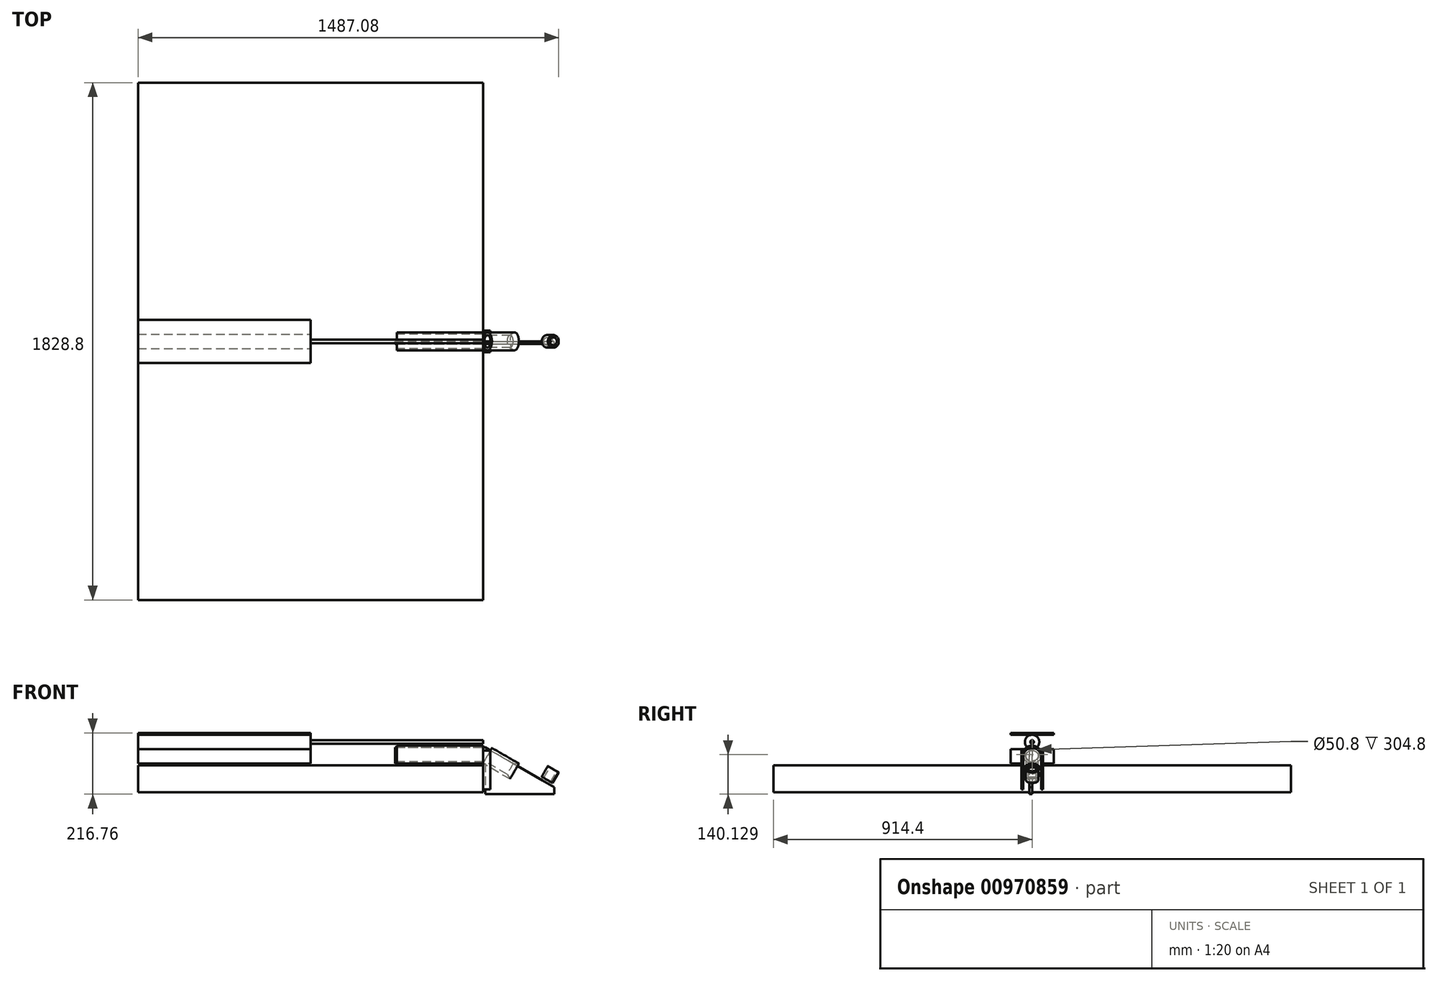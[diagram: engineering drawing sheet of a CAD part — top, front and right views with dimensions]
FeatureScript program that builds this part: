
annotation { "Feature Type Name" : "Feature", "Feature Type Description" : "" }
export const myFeature = defineFeature(function(context is Context, id is Id, definition is map)
    precondition{}
    {
        {
            var Q0;
            Q0=qCreatedBy(makeId("Front.planeOp"),FACE);
            var sketch = newSketch(context, id + "F0", { "sketchPlane" : qUnion([Q0])});
            skLineSegment(sketch, "E0.bottom", {"start": v(-592.75, 52.67) * mm, "end": v(16.85, 52.67) * mm});
            skLineSegment(sketch, "E0.top", {"start": v(-592.75, -48.93) * mm, "end": v(626.45, -48.93) * mm});
            skLineSegment(sketch, "E0.left", {"start": v(-592.75, 52.67) * mm, "end": v(-592.75, -48.93) * mm});
            skLineSegment(sketch, "E0.right", {"start": v(626.45, 52.67) * mm, "end": v(626.45, -48.93) * mm});
            skLineSegment(sketch, "E1.bottom", {"start": v(626.45, 52.67) * mm, "end": v(321.65, 52.67) * mm});
            skLineSegment(sketch, "E1.top", {"start": v(626.45, 116.17) * mm, "end": v(321.65, 116.17) * mm});
            skLineSegment(sketch, "E1.left", {"start": v(626.45, 52.67) * mm, "end": v(626.45, 116.17) * mm});
            skLineSegment(sketch, "E1.right", {"start": v(321.65, 52.67) * mm, "end": v(321.65, 116.17) * mm});
            skLineSegment(sketch, "E2.top", {"start": v(-592.75, 161.05) * mm, "end": v(16.85, 161.05) * mm});
            skLineSegment(sketch, "E2.left", {"start": v(-592.75, 52.67) * mm, "end": v(-592.75, 161.05) * mm});
            skLineSegment(sketch, "E2.right", {"start": v(16.85, 52.67) * mm, "end": v(16.85, 161.05) * mm});
            skLineSegment(sketch, "E3", {"start": v(626.45, 52.67) * mm, "end": v(802.43, -48.93) * mm});
            skLineSegment(sketch, "E4", {"start": v(802.43, -48.93) * mm, "end": v(834.18, 6.06) * mm});
            skLineSegment(sketch, "E5", {"start": v(626.45, 52.67) * mm, "end": v(658.2, 107.66) * mm});
            skLineSegment(sketch, "E6", {"start": v(658.2, 107.66) * mm, "end": v(834.18, 6.06) * mm});
            skLineSegment(sketch, "E7", {"start": v(834.18, 6.06) * mm, "end": v(834.18, 315.51) * mm});
            skLineSegment(sketch, "E8", {"start": v(554.78, 322.17) * mm, "end": v(554.78, 135.22) * mm});
            skLineSegment(sketch, "E9", {"start": v(626.45, 122.52) * mm, "end": v(16.85, 122.52) * mm});
            skLineSegment(sketch, "E10.0", {"start": v(626.45, 135.22) * mm, "end": v(16.85, 135.22) * mm});
            skLineSegment(sketch, "E11.0", {"start": v(665.46, 103.47) * mm, "end": v(655.78, 103.47) * mm});
            skLineSegment(sketch, "E12", {"start": v(16.85, 154.27) * mm, "end": v(16.85, 103.47) * mm});
            skLineSegment(sketch, "E13.trimOffspring", {"start": v(16.85, 154.27) * mm, "end": v(-592.75, 154.27) * mm});
            skLineSegment(sketch, "E14.trimOffspring", {"start": v(16.85, 103.47) * mm, "end": v(-592.75, 103.47) * mm});
            skLineSegment(sketch, "E15", {"start": v(626.45, 116.17) * mm, "end": v(626.45, 116.17) * mm});
            skLineSegment(sketch, "E16", {"start": v(626.45, 122.52) * mm, "end": v(626.45, 135.22) * mm});
            skLineSegment(sketch, "E17", {"start": v(834.18, 6.06) * mm, "end": v(855.85, 43.6) * mm});
            skLineSegment(sketch, "E18", {"start": v(855.85, 43.6) * mm, "end": v(894.18, 21.47) * mm});
            skLineSegment(sketch, "E19", {"start": v(894.18, 21.47) * mm, "end": v(872.45, -16.18) * mm});
            skLineSegment(sketch, "E20", {"start": v(872.45, -16.18) * mm, "end": v(834.18, 6.06) * mm});
            skLineSegment(sketch, "E21", {"start": v(853.31, -5.06) * mm, "end": v(834.18, -38.2) * mm});
            skLineSegment(sketch, "E22.0", {"start": v(-592.75, 46.32) * mm, "end": v(626.45, 46.32) * mm});
            skLineSegment(sketch, "E23.trimOffspring", {"start": v(321.65, 52.67) * mm, "end": v(626.45, 52.67) * mm});
            skLineSegment(sketch, "E24", {"start": v(321.65, 84.42) * mm, "end": v(626.45, 84.42) * mm});
            skLineSegment(sketch, "E25", {"start": v(642.33, 80.17) * mm, "end": v(818.3, -21.43) * mm});
            skLineSegment(sketch, "E26", {"start": v(853.31, -5.06) * mm, "end": v(875.12, 32.47) * mm});
            skLineSegment(sketch, "E27", {"start": v(626.45, 128.87) * mm, "end": v(16.85, 128.87) * mm});
            skLineSegment(sketch, "E28", {"start": v(16.85, 128.87) * mm, "end": v(-592.75, 128.87) * mm});
            skLineSegment(sketch, "E29.0", {"start": v(315.3, 52.67) * mm, "end": v(315.3, 109.82) * mm});
            skLineSegment(sketch, "E30", {"start": v(315.3, 52.67) * mm, "end": v(365.35, 52.67) * mm});
            skLineSegment(sketch, "E31", {"start": v(315.3, 109.82) * mm, "end": v(634.38, 109.82) * mm});
            skLineSegment(sketch, "E32", {"start": v(315.3, 52.67) * mm, "end": v(1006.93, 52.67) * mm});
            skLineSegment(sketch, "E33", {"start": v(634.38, 109.82) * mm, "end": v(634.38, -55.71) * mm});
            skLineSegment(sketch, "E34", {"start": v(880.35, 69.65) * mm, "end": v(877.52, 64.75) * mm});
            skLineSegment(sketch, "E35", {"start": v(877.52, 64.75) * mm, "end": v(779.96, -104.23) * mm});
            skLineSegment(sketch, "E36", {"start": v(634.38, -55.71) * mm, "end": v(824.21, -55.71) * mm});
            skLineSegment(sketch, "E37", {"start": v(634.38, 109.82) * mm, "end": v(836.25, -6.73) * mm});
            skLineSegment(sketch, "E38.0", {"start": v(912.5, 44.56) * mm, "end": v(814.93, -124.42) * mm});
            skLineSegment(sketch, "E39", {"start": v(836.25, -6.73) * mm, "end": v(878.82, -31.47) * mm});
            skLineSegment(sketch, "E40", {"start": v(824.21, -55.71) * mm, "end": v(878.82, -55.71) * mm});
            skLineSegment(sketch, "E41", {"start": v(878.82, -55.71) * mm, "end": v(878.82, -31.47) * mm});
            skSolve(sketch);
        }
        {
            var Q0;
            {var subQ0=sQuery(id+"F0.wireOp",EDGE,"E11.0");Q0=makeQuery(id+"F0.imprint","IMPRINT",FACE,{"disambiguationData":[TD([[makeQuery(id+"F0.imprint","IMPRINT",EDGE,{"derivedFrom":subQ0}),1.0]])]});}
            var Q1;
            {var subQ3=sQuery(id+"F0.wireOp",EDGE,"E11.0");Q1=makeQuery(id+"F0.imprint","IMPRINT",FACE,{"disambiguationData":[TD([[makeQuery(id+"F0.imprint","IMPRINT",EDGE,{"derivedFrom":subQ3}),-1.0]])]});}
            var Q2;
            Q2=sQuery(id+"F0.wireOp",EDGE,"E25");
            revolve(context, id + "F1", {"surfaceOperationType" : NewSurfaceOperationType.NEW, "entities" : qUnion([Q0, Q1]), "axis" : qUnion([Q2]), "revolveType" : RevolveType.FULL});
        }
        {
            var Q0;
            {var subQ0=sQuery(id+"F0.wireOp",EDGE,"E1.top");Q0=makeQuery(id+"F0.imprint","IMPRINT",FACE,{"disambiguationData":[TD([[makeQuery(id+"F0.imprint","IMPRINT",EDGE,{"derivedFrom":subQ0}),1.0]])]});}
            var Q1;
            Q1=sQuery(id+"F0.wireOp",EDGE,"E24");
            revolve(context, id + "F2", {"surfaceOperationType" : NewSurfaceOperationType.NEW, "entities" : qUnion([Q0]), "axis" : qUnion([Q1]), "revolveType" : RevolveType.FULL});
        }
        {
            var Q0;
            {var subQ0=sQuery(id+"F0.wireOp",EDGE,"E17");Q0=makeQuery(id+"F0.imprint","IMPRINT",FACE,{"disambiguationData":[TD([[makeQuery(id+"F0.imprint","IMPRINT",EDGE,{"derivedFrom":subQ0}),-1.0]])]});}
            var Q1;
            Q1=sQuery(id+"F0.wireOp",EDGE,"E26");
            revolve(context, id + "F3", {"surfaceOperationType" : NewSurfaceOperationType.NEW, "entities" : qUnion([Q0]), "axis" : qUnion([Q1]), "revolveType" : RevolveType.FULL});
        }
        {
            var Q0;
            {var subQ3=sQuery(id+"F0.wireOp",EDGE,"E13.trimOffspring");Q0=makeQuery(id+"F0.imprint","IMPRINT",FACE,{"disambiguationData":[TD([[makeQuery(id+"F0.imprint","IMPRINT",EDGE,{"derivedFrom":subQ3}),1.0]])]});}
            var Q1;
            Q1=sQuery(id+"F0.wireOp",EDGE,"E28");
            revolve(context, id + "F4", {"surfaceOperationType" : NewSurfaceOperationType.NEW, "entities" : qUnion([Q0]), "axis" : qUnion([Q1]), "revolveType" : RevolveType.FULL});
        }
        {
            var Q0;
            {var subQ3=sQuery(id+"F0.wireOp",EDGE,"E27");Q0=makeQuery(id+"F0.imprint","IMPRINT",FACE,{"disambiguationData":[TD([[makeQuery(id+"F0.imprint","IMPRINT",EDGE,{"derivedFrom":subQ3}),-1.0]])]});}
            var Q1;
            Q1=sQuery(id+"F0.wireOp",EDGE,"E27");
            revolve(context, id + "F5", {"operationType" : NewBodyOperationType.ADD, "surfaceOperationType" : NewSurfaceOperationType.NEW, "entities" : qUnion([Q0]), "axis" : qUnion([Q1]), "revolveType" : RevolveType.FULL});
        }
        {
            var Q0;
            {var subQ0=sQuery(id+"F0.wireOp",EDGE,"E2.top");Q0=makeQuery(id+"F0.imprint","IMPRINT",FACE,{"disambiguationData":[TD([[makeQuery(id+"F0.imprint","IMPRINT",EDGE,{"derivedFrom":subQ0}),-1.0]])]});}
            var Q1;
            {var subQ0=sQuery(id+"F0.wireOp",EDGE,"E0.bottom");Q1=makeQuery(id+"F0.imprint","IMPRINT",FACE,{"disambiguationData":[TD([[makeQuery(id+"F0.imprint","IMPRINT",EDGE,{"derivedFrom":subQ0}),1.0]])]});}
            extrude(context, id + "F6", {"entities" : qUnion([Q0, Q1]), "operationType" : NewBodyOperationType.ADD, "depth" : 152.4 * mm, "offsetDistance" : 25.4 * mm, "symmetric" : true});
        }
        {
            var Q0;
            {var subQ0=sQuery(id+"F0.wireOp",EDGE,"E0.top");Q0=makeQuery(id+"F0.imprint","IMPRINT",FACE,{"disambiguationData":[TD([[makeQuery(id+"F0.imprint","IMPRINT",EDGE,{"derivedFrom":subQ0}),1.0]])]});}
            extrude(context, id + "F7", {"entities" : qUnion([Q0]), "depth" : 1828.8 * mm, "offsetDistance" : 25.4 * mm, "symmetric" : true});
        }
        {
            var Q0;
            Q0=makeQuery(id+"F2.opRevolve","SWEPT_FACE",FACE,{"disambiguationData":[OSD([sQuery(id+"F0.wireOp",EDGE,"E1.left")])]});
            var sketch = newSketch(context, id + "F8", { "sketchPlane" : qUnion([Q0])});
            skLineSegment(sketch, "E42", {"start": v(31.75, 97.95) * mm, "end": v(31.75, -14.33) * mm});
            skLineSegment(sketch, "E43", {"start": v(-31.75, 97.95) * mm, "end": v(-31.75, -38.39) * mm});
            skLineSegment(sketch, "E44", {"start": v(-31.75, 177.43) * mm, "end": v(-38.1, 177.43) * mm});
            skLineSegment(sketch, "E45", {"start": v(-38.1, 97.95) * mm, "end": v(-38.1, -38.39) * mm});
            skLineSegment(sketch, "E46", {"start": v(31.75, 175.71) * mm, "end": v(38.1, 175.71) * mm});
            skLineSegment(sketch, "E47", {"start": v(38.1, 97.95) * mm, "end": v(38.1, -38.39) * mm});
            skLineSegment(sketch, "E48", {"start": v(31.75, -38.39) * mm, "end": v(31.75, -14.33) * mm});
            skLineSegment(sketch, "E49", {"start": v(38.1, -38.39) * mm, "end": v(31.75, -38.39) * mm});
            skLineSegment(sketch, "E50.trimOffspring", {"start": v(-31.75, -38.39) * mm, "end": v(-38.1, -38.39) * mm});
            skPoint(sketch, "E51.end.orphan", {"position": v(31.75, -54) * mm});
            skLineSegment(sketch, "E52", {"start": v(38.1, 97.95) * mm, "end": v(31.75, 97.95) * mm});
            skLineSegment(sketch, "E53.trimOffspring", {"start": v(-31.75, 97.95) * mm, "end": v(-38.1, 97.95) * mm});
            skSolve(sketch);
        }
        {
            var Q0;
            Q0=makeQuery(id+"F8.imprint","IMPRINT",FACE,{"disambiguationData":[TD([[makeQuery(id+"F8.imprint","IMPRINT",EDGE,{"derivedFrom":sQuery(id+"F8.wireOp",EDGE,"E45")}),1.0]])]});
            var Q1;
            Q1=makeQuery(id+"F8.imprint","IMPRINT",FACE,{"disambiguationData":[TD([[makeQuery(id+"F8.imprint","IMPRINT",EDGE,{"derivedFrom":sQuery(id+"F8.wireOp",EDGE,"E47")}),-1.0]])]});
            extrude(context, id + "F9", {"entities" : qUnion([Q0, Q1]), "depth" : 25.4 * mm, "offsetDistance" : 25.4 * mm});
        }
        {
            var Q0;
            {var subQ0=sQuery(id+"F0.wireOp",EDGE,"E24");Q0=makeQuery(id+"F0.imprint","IMPRINT",FACE,{"disambiguationData":[TD([[makeQuery(id+"F0.imprint","IMPRINT",EDGE,{"derivedFrom":subQ0}),1.0]])]});}
            var Q1;
            {var subQ1=sQuery(id+"F0.wireOp",EDGE,"E29.0");Q1=makeQuery(id+"F0.imprint","IMPRINT",FACE,{"disambiguationData":[TD([[makeQuery(id+"F0.imprint","IMPRINT",EDGE,{"derivedFrom":subQ1}),-1.0]])]});}
            var Q2;
            {var subQ3=sQuery(id+"F0.wireOp",EDGE,"E24");Q2=makeQuery(id+"F0.imprint","IMPRINT",FACE,{"disambiguationData":[TD([[makeQuery(id+"F0.imprint","IMPRINT",EDGE,{"derivedFrom":subQ3}),-1.0]])]});}
            var Q3;
            {var subQ3=sQuery(id+"F0.wireOp",EDGE,"E1.left");var subQ8=makeQuery(id+"F0.imprint","INTERSECT",VERTEX,{"derivedFrom":[subQ3,sQuery(id+"F0.wireOp",EDGE,"E24")]});Q3=makeQuery(id+"F0.imprint","IMPRINT",FACE,{"disambiguationData":[TD([[makeQuery(id+"F0.imprint","IMPRINT",EDGE,{"disambiguationData":[TD([[subQ8,-1.0]])],"derivedFrom":subQ3}),-1.0]])]});}
            var Q4;
            {var subQ0=sQuery(id+"F0.wireOp",EDGE,"E5");var subQ1=makeQuery(id+"F0.imprint","INTERSECT",VERTEX,{"derivedFrom":[subQ0,sQuery(id+"F0.wireOp",EDGE,"E25")]});Q4=makeQuery(id+"F0.imprint","IMPRINT",FACE,{"disambiguationData":[TD([[makeQuery(id+"F0.imprint","IMPRINT",EDGE,{"disambiguationData":[TD([[subQ1,1.0]])],"derivedFrom":subQ0}),1.0]])]});}
            var Q5;
            {var subQ0=sQuery(id+"F0.wireOp",EDGE,"E25");var subQ1=sQuery(id+"F0.wireOp",EDGE,"E5");var subQ2=makeQuery(id+"F0.imprint","INTERSECT",VERTEX,{"derivedFrom":[subQ1,subQ0]});Q5=makeQuery(id+"F0.imprint","IMPRINT",FACE,{"disambiguationData":[TD([[makeQuery(id+"F0.imprint","IMPRINT",EDGE,{"disambiguationData":[TD([[subQ2,-1.0]])],"derivedFrom":subQ1}),-1.0]])]});}
            var Q6;
            {var subQ0=sQuery(id+"F0.wireOp",EDGE,"E25");var subQ1=sQuery(id+"F0.wireOp",EDGE,"E5");var subQ2=makeQuery(id+"F0.imprint","INTERSECT",VERTEX,{"derivedFrom":[subQ1,subQ0]});Q6=makeQuery(id+"F0.imprint","IMPRINT",FACE,{"disambiguationData":[TD([[makeQuery(id+"F0.imprint","IMPRINT",EDGE,{"disambiguationData":[TD([[subQ2,1.0]])],"derivedFrom":subQ1}),-1.0]])]});}
            var Q7;
            {var subQ1=sQuery(id+"F0.wireOp",EDGE,"E5");var subQ3=sQuery(id+"F0.wireOp",EDGE,"E33");var subQ4=makeQuery(id+"F0.imprint","INTERSECT",VERTEX,{"derivedFrom":[subQ1,subQ3]});Q7=makeQuery(id+"F0.imprint","IMPRINT",FACE,{"disambiguationData":[TD([[makeQuery(id+"F0.imprint","IMPRINT",EDGE,{"disambiguationData":[TD([[subQ4,-1.0]])],"derivedFrom":subQ3}),-1.0]])]});}
            var Q8;
            {var subQ0=sQuery(id+"F0.wireOp",EDGE,"E4");var subQ7=sQuery(id+"F0.wireOp",EDGE,"E3");var subQ9=makeQuery(id+"F0.imprint","INTERSECT",VERTEX,{"derivedFrom":[subQ7,subQ0]});Q8=makeQuery(id+"F0.imprint","IMPRINT",FACE,{"disambiguationData":[TD([[makeQuery(id+"F0.imprint","IMPRINT",EDGE,{"disambiguationData":[TD([[subQ9,1.0]])],"derivedFrom":subQ7}),-1.0]])]});}
            var Q9;
            {var subQ5=sQuery(id+"F0.wireOp",EDGE,"E4");var subQ7=sQuery(id+"F0.wireOp",EDGE,"E3");var subQ8=makeQuery(id+"F0.imprint","INTERSECT",VERTEX,{"derivedFrom":[subQ7,subQ5]});Q9=makeQuery(id+"F0.imprint","IMPRINT",FACE,{"disambiguationData":[TD([[makeQuery(id+"F0.imprint","IMPRINT",EDGE,{"disambiguationData":[TD([[subQ8,1.0]])],"derivedFrom":subQ7}),1.0]])]});}
            var Q10;
            {var subQ0=sQuery(id+"F0.wireOp",EDGE,"E25");var subQ1=sQuery(id+"F0.wireOp",EDGE,"E4");var subQ2=makeQuery(id+"F0.imprint","INTERSECT",VERTEX,{"derivedFrom":[subQ1,subQ0]});Q10=makeQuery(id+"F0.imprint","IMPRINT",FACE,{"disambiguationData":[TD([[makeQuery(id+"F0.imprint","IMPRINT",EDGE,{"disambiguationData":[TD([[subQ2,-1.0]])],"derivedFrom":subQ1}),1.0]])]});}
            var Q11;
            {var subQ6=sQuery(id+"F0.wireOp",EDGE,"E40");var subQ8=sQuery(id+"F0.wireOp",EDGE,"E36");var subQ9=makeQuery(id+"F0.imprint","INTERSECT",VERTEX,{"derivedFrom":[subQ8,subQ6]});Q11=makeQuery(id+"F0.imprint","IMPRINT",FACE,{"disambiguationData":[TD([[makeQuery(id+"F0.imprint","IMPRINT",EDGE,{"disambiguationData":[TD([[subQ9,1.0]])],"derivedFrom":subQ8}),1.0]])]});}
            var Q12;
            {var subQ5=sQuery(id+"F0.wireOp",EDGE,"E41");Q12=makeQuery(id+"F0.imprint","IMPRINT",FACE,{"disambiguationData":[TD([[makeQuery(id+"F0.imprint","IMPRINT",EDGE,{"derivedFrom":subQ5}),1.0]])]});}
            extrude(context, id + "F10", {"entities" : qUnion([Q0, Q1, Q2, Q3, Q4, Q5, Q6, Q7, Q8, Q9, Q10, Q11, Q12]), "depth" : 9.52 * mm, "offsetDistance" : 25.4 * mm});
        }
    });
